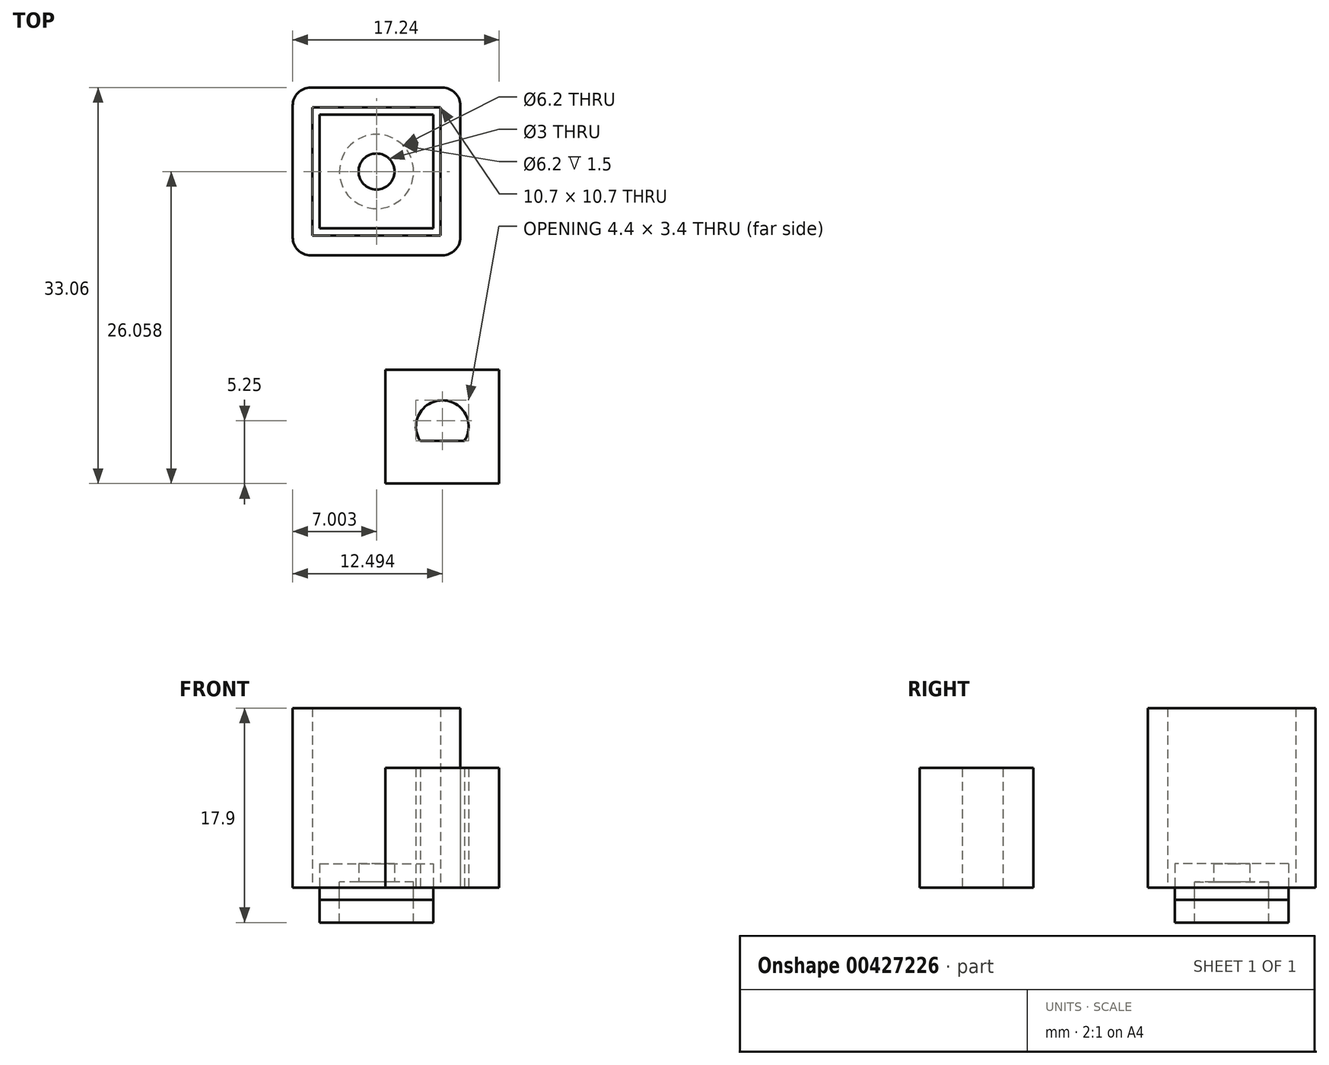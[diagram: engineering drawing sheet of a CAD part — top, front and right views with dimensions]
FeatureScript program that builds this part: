
annotation { "Feature Type Name" : "Feature", "Feature Type Description" : "" }
export const myFeature = defineFeature(function(context is Context, id is Id, definition is map)
    precondition{}
    {
        {
            var Q0;
            Q0=qCreatedBy(makeId("Top.planeOp"),FACE);
            var sketch = newSketch(context, id + "F0", { "sketchPlane" : qUnion([Q0])});
            skCircle(sketch, "E0", {"center": v(8.24, -15.63) * mm, "radius": 7.5 * mm});
            skLineSegment(sketch, "E1", {"start": v(11.1, -14.71) * mm, "end": v(6.03, -13.6) * mm});
            skArc(sketch, "E2", {"start": v(6.03, -13.6) * mm, "mid": v(7.6, -18.56) * mm, "end": v(11.1, -14.71) * mm});
            skSolve(sketch);
        }
        {
            var Q0;
            Q0=makeQuery(id+"F0.imprint","IMPRINT",FACE,{"disambiguationData":[TD([[makeQuery(id+"F0.imprint","IMPRINT",EDGE,{"derivedFrom":sQuery(id+"F0.wireOp",EDGE,"E0")}),1.0]])]});
            extrude(context, id + "F1", {"entities" : qUnion([Q0]), "depth" : 20 * mm});
        }
        {
            var Q0;
            Q0=makeQuery(id+"F1.opExtrude","CAP_FACE",FACE,{"disambiguationData":[OSD([sQuery(id+"F0.wireOp",EDGE,"dWDlLjBw-SzBN-feQ3-MVoI-kTcs59UhA39O"),sQuery(id+"F0.wireOp",EDGE,"E0")])],"isStart":false});
            var sketch = newSketch(context, id + "F2", { "sketchPlane" : qUnion([Q0])});
            skLineSegment(sketch, "E3.bottom", {"start": v(18.24, -23.13) * mm, "end": v(-1.76, -23.13) * mm});
            skLineSegment(sketch, "E3.top", {"start": v(18.24, -8.13) * mm, "end": v(-1.76, -8.13) * mm});
            skLineSegment(sketch, "E3.left", {"start": v(18.24, -23.13) * mm, "end": v(18.24, -8.13) * mm});
            skLineSegment(sketch, "E3.right", {"start": v(-1.76, -23.13) * mm, "end": v(-1.76, -8.13) * mm});
            skPoint(sketch, "E3.middle", {"position": v(8.24, -15.63) * mm});
            skSolve(sketch);
        }
        {
            var Q0;
            {var subQ0=sQuery(id+"F2.wireOp",EDGE,"E3.right");Q0=makeQuery(id+"F2.imprint","IMPRINT",FACE,{"disambiguationData":[TD([[makeQuery(id+"F2.imprint","IMPRINT",EDGE,{"derivedFrom":subQ0}),-1.0]])]});}
            var Q1;
            Q1=makeQuery(id+"F2.imprint","IMPRINT",FACE,{"disambiguationData":[TD([[makeQuery(id+"F2.imprint","IMPRINT",EDGE,{"derivedFrom":makeQuery(id+"F1.opExtrude","CAP_EDGE",EDGE,{"disambiguationData":[OSD([sQuery(id+"F0.wireOp",EDGE,"dWDlLjBw-SzBN-feQ3-MVoI-kTcs59UhA39O")])],"isStart":false})}),-1.0]])]});
            var Q2;
            {var subQ0=sQuery(id+"F2.wireOp",EDGE,"E3.left");Q2=makeQuery(id+"F2.imprint","IMPRINT",FACE,{"disambiguationData":[TD([[makeQuery(id+"F2.imprint","IMPRINT",EDGE,{"derivedFrom":subQ0}),1.0]])]});}
            var Q3;
            Q3=makeQuery(id+"F2.imprint","IMPRINT",FACE,{"disambiguationData":[TD([[makeQuery(id+"F2.imprint","IMPRINT",EDGE,{"derivedFrom":makeQuery(id+"F1.opExtrude","CAP_EDGE",EDGE,{"disambiguationData":[OSD([sQuery(id+"F0.wireOp",EDGE,"dWDlLjBw-SzBN-feQ3-MVoI-kTcs59UhA39O")])],"isStart":false})}),1.0]])]});
            extrude(context, id + "F3", {"entities" : qUnion([Q0, Q1, Q2, Q3]), "operationType" : NewBodyOperationType.ADD, "oppositeDirection" : true, "depth" : 20 * mm});
        }
        {
            var Q0;
            Q0=makeQuery(id+"F3.opExtrude","CAP_FACE",FACE,{"disambiguationData":[OSD([sQuery(id+"F2.wireOp",EDGE,"E3.bottom"),sQuery(id+"F2.wireOp",EDGE,"E3.top"),sQuery(id+"F2.wireOp",EDGE,"E3.left"),sQuery(id+"F2.wireOp",EDGE,"E3.right")])],"isStart":false});
            var sketch = newSketch(context, id + "F4", { "sketchPlane" : qUnion([Q0])});
            skPoint(sketch, "E4.middle", {"position": v(8.24, 15.63) * mm});
            skPoint(sketch, "E4.middle.positionSnap1", {"position": v(8.24, 8.13) * mm});
            skPoint(sketch, "E4.centerSnap1", {"position": v(8.24, 8.13) * mm});
            skLineSegment(sketch, "E5", {"start": v(20.74, 12.63) * mm, "end": v(20.74, 18.63) * mm});
            skLineSegment(sketch, "E6", {"start": v(8.24, 19.63) * mm, "end": v(8.24, 11.63) * mm});
            skLineSegment(sketch, "E7", {"start": v(8.24, 15.63) * mm, "end": v(20.74, 15.63) * mm});
            skLineSegment(sketch, "E8", {"start": v(20.74, 12.63) * mm, "end": v(8.24, 11.63) * mm});
            skLineSegment(sketch, "E9", {"start": v(20.74, 18.63) * mm, "end": v(8.24, 19.63) * mm});
            skLineSegment(sketch, "E10.MirrorCS", {"start": v(-4.26, 12.63) * mm, "end": v(8.24, 11.63) * mm});
            skLineSegment(sketch, "E11.MirrorCS", {"start": v(-4.26, 12.63) * mm, "end": v(-4.26, 18.63) * mm});
            skLineSegment(sketch, "E12.MirrorCS", {"start": v(-4.26, 18.63) * mm, "end": v(8.24, 19.63) * mm});
            skSolve(sketch);
        }
        {
            var Q0;
            {var subQ0=sQuery(id+"F4.wireOp",EDGE,"E7");var subQ1=makeQuery(id+"F1.opExtrude","CAP_EDGE",EDGE,{"disambiguationData":[OSD([sQuery(id+"F0.wireOp",EDGE,"E2")])],"isStart":true});var subQ2=makeQuery(id+"F4.imprint","INTERSECT",VERTEX,{"derivedFrom":[subQ1,subQ0]});Q0=makeQuery(id+"F4.imprint","IMPRINT",FACE,{"disambiguationData":[TD([[makeQuery(id+"F4.imprint","IMPRINT",EDGE,{"disambiguationData":[TD([[subQ2,-1.0]])],"derivedFrom":subQ0}),-1.0]])]});}
            var Q1;
            {var subQ1=makeQuery(id+"F1.opExtrude","CAP_EDGE",EDGE,{"disambiguationData":[OSD([sQuery(id+"F0.wireOp",EDGE,"E2")])],"isStart":true});var subQ3=sQuery(id+"F4.wireOp",EDGE,"E7");var subQ4=makeQuery(id+"F4.imprint","INTERSECT",VERTEX,{"derivedFrom":[subQ1,subQ3]});Q1=makeQuery(id+"F4.imprint","IMPRINT",FACE,{"disambiguationData":[TD([[makeQuery(id+"F4.imprint","IMPRINT",EDGE,{"disambiguationData":[TD([[subQ4,-1.0]])],"derivedFrom":subQ3}),1.0]])]});}
            var Q2;
            {var subQ7=makeQuery(id+"F1.opExtrude","CAP_EDGE",EDGE,{"disambiguationData":[OSD([sQuery(id+"F0.wireOp",EDGE,"E1")])],"isStart":true});var subQ10=makeQuery(id+"F1.opExtrude","CAP_EDGE",EDGE,{"disambiguationData":[OSD([sQuery(id+"F0.wireOp",EDGE,"E2")])],"isStart":true});var subQ12=makeQuery(id+"F4.imprint","INTERSECT",VERTEX,{"disambiguationData":[OD(1.0)],"derivedFrom":[subQ7,subQ10]});Q2=makeQuery(id+"F4.imprint","IMPRINT",FACE,{"disambiguationData":[TD([[makeQuery(id+"F4.imprint","IMPRINT",EDGE,{"disambiguationData":[TD([[subQ12,1.0]])],"derivedFrom":subQ7}),1.0]])]});}
            extrude(context, id + "F5", {"entities" : qUnion([Q0, Q1, Q2]), "operationType" : NewBodyOperationType.REMOVE, "oppositeDirection" : true, "depth" : 5 * mm});
        }
        {
            var Q0;
            Q0=qCreatedBy(makeId("Top.planeOp"),FACE);
            var sketch = newSketch(context, id + "F6", { "sketchPlane" : qUnion([Q0])});
            skCircle(sketch, "E13", {"center": v(48.83, -13.54) * mm, "radius": 10 * mm});
            skLineSegment(sketch, "E14", {"start": v(48.83, -13.54) * mm, "end": v(48.83, -11.34) * mm});
            skLineSegment(sketch, "E15", {"start": v(48.83, -13.54) * mm, "end": v(48.83, -14.74) * mm});
            skArc(sketch, "E16", {"start": v(50.68, -14.74) * mm, "mid": v(48.83, -11.34) * mm, "end": v(47, -14.74) * mm});
            skLineSegment(sketch, "E17", {"start": v(50.68, -14.74) * mm, "end": v(47, -14.74) * mm});
            skLineSegment(sketch, "E18.bottom", {"start": v(44.08, -8.79) * mm, "end": v(53.58, -8.79) * mm});
            skLineSegment(sketch, "E18.top", {"start": v(44.08, -18.29) * mm, "end": v(53.58, -18.29) * mm});
            skLineSegment(sketch, "E18.left", {"start": v(44.08, -8.79) * mm, "end": v(44.08, -18.29) * mm});
            skLineSegment(sketch, "E18.right", {"start": v(53.58, -8.79) * mm, "end": v(53.58, -18.29) * mm});
            skSolve(sketch);
        }
        {
            var Q0;
            Q0=qCreatedBy(makeId("Top.planeOp"),FACE);
            var sketch = newSketch(context, id + "F7", { "sketchPlane" : qUnion([Q0])});
            skCircle(sketch, "E19", {"center": v(43.34, 7.77) * mm, "radius": 10 * mm});
            skLineSegment(sketch, "E20.bottom", {"start": v(38.6, 12.52) * mm, "end": v(48.1, 12.52) * mm});
            skLineSegment(sketch, "E20.top", {"start": v(38.6, 3.02) * mm, "end": v(48.1, 3.02) * mm});
            skLineSegment(sketch, "E20.left", {"start": v(38.6, 12.52) * mm, "end": v(38.6, 3.02) * mm});
            skLineSegment(sketch, "E20.right", {"start": v(48.1, 12.52) * mm, "end": v(48.1, 3.02) * mm});
            skLineSegment(sketch, "E21.bottom", {"start": v(37.84, 14.77) * mm, "end": v(48.84, 14.77) * mm});
            skLineSegment(sketch, "E21.top", {"start": v(37.84, 0.77) * mm, "end": v(48.84, 0.77) * mm});
            skLineSegment(sketch, "E21.left", {"start": v(36.34, 13.27) * mm, "end": v(36.34, 2.27) * mm});
            skLineSegment(sketch, "E21.right", {"start": v(50.34, 13.27) * mm, "end": v(50.34, 2.27) * mm});
            skPoint(sketch, "E22.visualSharp", {"position": v(50.34, 14.77) * mm});
            skArc(sketch, "E22.filletArc", {"start": v(50.34, 13.27) * mm, "mid": v(49.9, 14.33) * mm, "end": v(48.84, 14.77) * mm});
            skPoint(sketch, "E23.visualSharp", {"position": v(36.34, 14.77) * mm});
            skArc(sketch, "E23.filletArc", {"start": v(37.84, 14.77) * mm, "mid": v(36.78, 14.33) * mm, "end": v(36.34, 13.27) * mm});
            skPoint(sketch, "E24.visualSharp", {"position": v(36.34, 0.77) * mm});
            skArc(sketch, "E24.filletArc", {"start": v(36.34, 2.27) * mm, "mid": v(36.78, 1.2) * mm, "end": v(37.84, 0.77) * mm});
            skPoint(sketch, "E25.visualSharp", {"position": v(50.34, 0.77) * mm});
            skArc(sketch, "E25.filletArc", {"start": v(48.84, 0.77) * mm, "mid": v(49.9, 1.2) * mm, "end": v(50.34, 2.27) * mm});
            skCircle(sketch, "E26", {"center": v(43.34, 7.77) * mm, "radius": 3.1 * mm});
            skCircle(sketch, "E27", {"center": v(43.34, 7.77) * mm, "radius": 1.5 * mm});
            skCircle(sketch, "E28", {"center": v(43.34, 7.77) * mm, "radius": 4.35 * mm});
            skLineSegment(sketch, "E29.bottom", {"start": v(38, 2.42) * mm, "end": v(48.7, 2.42) * mm});
            skLineSegment(sketch, "E29.top", {"start": v(38, 13.12) * mm, "end": v(48.7, 13.12) * mm});
            skLineSegment(sketch, "E29.left", {"start": v(38, 2.42) * mm, "end": v(38, 13.12) * mm});
            skLineSegment(sketch, "E29.right", {"start": v(48.7, 2.42) * mm, "end": v(48.7, 13.12) * mm});
            skSolve(sketch);
        }
        {
            var Q0;
            Q0=makeQuery(id+"F7.imprint","IMPRINT",FACE,{"disambiguationData":[TD([[makeQuery(id+"F7.imprint","IMPRINT",EDGE,{"derivedFrom":sQuery(id+"F7.wireOp",EDGE,"E26")}),-1.0]])]});
            var Q1;
            Q1=makeQuery(id+"F7.imprint","IMPRINT",FACE,{"disambiguationData":[TD([[makeQuery(id+"F7.imprint","IMPRINT",EDGE,{"derivedFrom":sQuery(id+"F7.wireOp",EDGE,"E20.bottom")}),-1.0]])]});
            extrude(context, id + "F8", {"entities" : qUnion([Q0, Q1]), "oppositeDirection" : true, "depth" : 2.9 * mm});
        }
        {
            var Q0;
            Q0=makeQuery(id+"F8.opExtrude","CAP_FACE",FACE,{"disambiguationData":[OSD([sQuery(id+"F7.wireOp",EDGE,"E28")])],"isStart":true});
            var Q1;
            Q1=makeQuery(id+"F7.imprint","IMPRINT",FACE,{"disambiguationData":[TD([[makeQuery(id+"F7.imprint","IMPRINT",EDGE,{"derivedFrom":sQuery(id+"F7.wireOp",EDGE,"E26")}),-1.0]])]});
            var Q2;
            {var subQ0=sQuery(id+"F7.wireOp",EDGE,"E20.left");var subQ1=sQuery(id+"F7.wireOp",EDGE,"E20.bottom");var subQ2=makeQuery(id+"F7.imprint","INTERSECT",VERTEX,{"derivedFrom":[subQ1,subQ0]});Q2=makeQuery(id+"F7.imprint","IMPRINT",FACE,{"disambiguationData":[TD([[makeQuery(id+"F7.imprint","IMPRINT",EDGE,{"disambiguationData":[TD([[subQ2,-1.0]])],"derivedFrom":subQ1}),-1.0]])]});}
            var Q3;
            {var subQ0=sQuery(id+"F7.wireOp",EDGE,"E20.left");var subQ1=sQuery(id+"F7.wireOp",EDGE,"E20.top");var subQ2=makeQuery(id+"F7.imprint","INTERSECT",VERTEX,{"derivedFrom":[subQ1,subQ0]});Q3=makeQuery(id+"F7.imprint","IMPRINT",FACE,{"disambiguationData":[TD([[makeQuery(id+"F7.imprint","IMPRINT",EDGE,{"disambiguationData":[TD([[subQ2,-1.0]])],"derivedFrom":subQ1}),1.0]])]});}
            var Q4;
            {var subQ0=sQuery(id+"F7.wireOp",EDGE,"E20.right");var subQ1=sQuery(id+"F7.wireOp",EDGE,"E20.bottom");var subQ2=makeQuery(id+"F7.imprint","INTERSECT",VERTEX,{"derivedFrom":[subQ1,subQ0]});Q4=makeQuery(id+"F7.imprint","IMPRINT",FACE,{"disambiguationData":[TD([[makeQuery(id+"F7.imprint","IMPRINT",EDGE,{"disambiguationData":[TD([[subQ2,1.0]])],"derivedFrom":subQ1}),-1.0]])]});}
            var Q5;
            {var subQ0=sQuery(id+"F7.wireOp",EDGE,"E20.right");var subQ1=sQuery(id+"F7.wireOp",EDGE,"E20.top");var subQ2=makeQuery(id+"F7.imprint","INTERSECT",VERTEX,{"derivedFrom":[subQ1,subQ0]});Q5=makeQuery(id+"F7.imprint","IMPRINT",FACE,{"disambiguationData":[TD([[makeQuery(id+"F7.imprint","IMPRINT",EDGE,{"disambiguationData":[TD([[subQ2,1.0]])],"derivedFrom":subQ1}),1.0]])]});}
            var Q6;
            Q6=makeQuery(id+"F7.imprint","IMPRINT",FACE,{"disambiguationData":[TD([[makeQuery(id+"F7.imprint","IMPRINT",EDGE,{"derivedFrom":sQuery(id+"F7.wireOp",EDGE,"E26")}),1.0]])]});
            extrude(context, id + "F9", {"entities" : qUnion([Q0, Q1, Q2, Q3, Q4, Q5, Q6]), "depth" : 2 * mm, "hasSecondDirection" : true, "secondDirectionOppositeDirection" : true, "secondDirectionDepth" : 1 * mm});
        }
        {
            var Q0;
            Q0=makeQuery(id+"F7.imprint","IMPRINT",FACE,{"disambiguationData":[TD([[makeQuery(id+"F7.imprint","IMPRINT",EDGE,{"derivedFrom":sQuery(id+"F7.wireOp",EDGE,"E26")}),1.0]])]});
            var Q1;
            Q1=makeQuery(id+"F7.imprint","IMPRINT",FACE,{"disambiguationData":[TD([[makeQuery(id+"F7.imprint","IMPRINT",EDGE,{"derivedFrom":sQuery(id+"F7.wireOp",EDGE,"E27")}),1.0]])]});
            extrude(context, id + "F10", {"entities" : qUnion([Q0, Q1]), "operationType" : NewBodyOperationType.REMOVE, "oppositeDirection" : true, "depth" : 25 * mm, "hasSecondDirection" : true, "secondDirectionOppositeDirection" : false, "secondDirectionDepth" : 0.5 * mm});
        }
        {
            var Q0;
            Q0=makeQuery(id+"F7.imprint","IMPRINT",FACE,{"disambiguationData":[TD([[makeQuery(id+"F7.imprint","IMPRINT",EDGE,{"derivedFrom":sQuery(id+"F7.wireOp",EDGE,"E27")}),1.0]])]});
            extrude(context, id + "F11", {"entities" : qUnion([Q0]), "operationType" : NewBodyOperationType.REMOVE, "depth" : 25 * mm, "hasSecondDirection" : true, "secondDirectionOppositeDirection" : true, "secondDirectionDepth" : 25 * mm});
        }
        {
            var Q0;
            Q0=makeQuery(id+"F6.imprint","IMPRINT",FACE,{"disambiguationData":[TD([[makeQuery(id+"F6.imprint","IMPRINT",EDGE,{"derivedFrom":sQuery(id+"F6.wireOp",EDGE,"E18.bottom")}),-1.0]])]});
            extrude(context, id + "F12", {"entities" : qUnion([Q0]), "depth" : 10 * mm});
        }
        {
            var Q0;
            Q0=makeQuery(id+"F1.opExtrude","SWEPT_BODY",BODY,{"disambiguationData":[OSD([sQuery(id+"F0.wireOp",EDGE,"E0"),sQuery(id+"F0.wireOp",EDGE,"E1"),sQuery(id+"F0.wireOp",EDGE,"E2")])]});
            deleteBodies(context, id + "F13", {"entities" : qUnion([Q0])});
        }
        {
            var Q0;
            Q0=makeQuery(id+"F7.imprint","IMPRINT",FACE,{"disambiguationData":[TD([[makeQuery(id+"F7.imprint","IMPRINT",EDGE,{"derivedFrom":sQuery(id+"F7.wireOp",EDGE,"E21.bottom")}),-1.0]])]});
            extrude(context, id + "F14", {"entities" : qUnion([Q0]), "depth" : 15 * mm});
        }
    });
